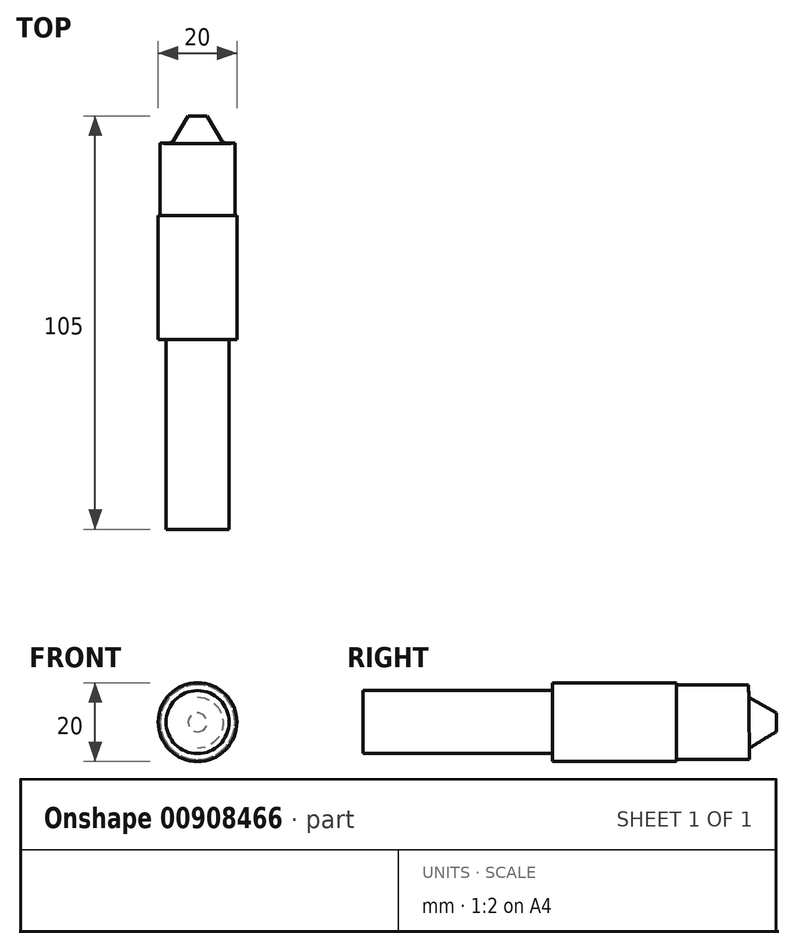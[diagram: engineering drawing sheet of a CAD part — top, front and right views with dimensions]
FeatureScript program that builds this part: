
annotation { "Feature Type Name" : "Feature", "Feature Type Description" : "" }
export const myFeature = defineFeature(function(context is Context, id is Id, definition is map)
    precondition{}
    {
        {
            var Q0;
            Q0=qCreatedBy(makeId("Front.planeOp"),FACE);
            var sketch = newSketch(context, id + "F0", { "sketchPlane" : qUnion([Q0])});
            skCircle(sketch, "E0", {"center": v(0, 0) * mm, "radius": 10 * mm});
            skSolve(sketch);
        }
        {
            var Q0;
            Q0 = qSketchRegion(id + "F0", true);
            extrude(context, id + "F1", {"entities" : qUnion([Q0]), "depth" : 105 * mm, "offsetDistance" : 25 * mm});
        }
        {
            var Q0;
            Q0=makeQuery(id+"F1.opExtrude","CAP_FACE",FACE,{"disambiguationData":[OSD([sQuery(id+"F0.wireOp",EDGE,"E0")])],"isStart":true});
            var sketch = newSketch(context, id + "F2", { "sketchPlane" : qUnion([Q0])});
            skCircle(sketch, "E1", {"center": v(0, 0) * mm, "radius": 9.5 * mm});
            skCircle(sketch, "E2", {"center": v(0, 0) * mm, "radius": 15.83 * mm});
            skSolve(sketch);
        }
        {
            var Q0;
            Q0 = qSketchRegion(id + "F2", true);
            extrude(context, id + "F3", {"entities" : qUnion([Q0]), "operationType" : NewBodyOperationType.REMOVE, "oppositeDirection" : true, "depth" : 25.3 * mm, "offsetDistance" : 25 * mm});
        }
        {
            var Q0;
            Q0=qCreatedBy(makeId("Right.planeOp"),FACE);
            var sketch = newSketch(context, id + "F4", { "sketchPlane" : qUnion([Q0])});
            skPoint(sketch, "E3", {"position": v(-7, 6.35) * mm});
            skLineSegment(sketch, "E4", {"start": v(-7, 6.35) * mm, "end": v(4, 0) * mm});
            skLineSegment(sketch, "E5", {"start": v(-7, 6.35) * mm, "end": v(-7, 17.07) * mm});
            skLineSegment(sketch, "E6", {"start": v(-7, 17.07) * mm, "end": v(6.7, 17.07) * mm});
            skLineSegment(sketch, "E7", {"start": v(6.7, 17.07) * mm, "end": v(6.9, 0.04) * mm});
            skLineSegment(sketch, "E8", {"start": v(4, 0) * mm, "end": v(6.9, 0.04) * mm});
            skSolve(sketch);
        }
        {
            var Q0;
            Q0 = qSketchRegion(id + "F4", true);
            var Q1;
            Q1=sQuery(id+"F4.wireOp",EDGE,"E8");
            revolve(context, id + "F5", {"operationType" : NewBodyOperationType.REMOVE, "surfaceOperationType" : NewSurfaceOperationType.NEW, "entities" : qUnion([Q0]), "axis" : qUnion([Q1]), "revolveType" : RevolveType.FULL, "oppositeDirection" : true});
        }
        {
            var Q0;
            Q0=makeQuery(id+"F1.opExtrude","CAP_FACE",FACE,{"disambiguationData":[OSD([sQuery(id+"F0.wireOp",EDGE,"E0")])],"isStart":false});
            var sketch = newSketch(context, id + "F6", { "sketchPlane" : qUnion([Q0])});
            skCircle(sketch, "E9", {"center": v(0, 0) * mm, "radius": 8 * mm});
            skCircle(sketch, "E10", {"center": v(0, 0) * mm, "radius": 17.93 * mm});
            skSolve(sketch);
        }
        {
            var Q0;
            Q0 = qSketchRegion(id + "F6", true);
            extrude(context, id + "F7", {"entities" : qUnion([Q0]), "operationType" : NewBodyOperationType.REMOVE, "oppositeDirection" : true, "depth" : 48.2 * mm, "offsetDistance" : 25 * mm});
        }
    });
